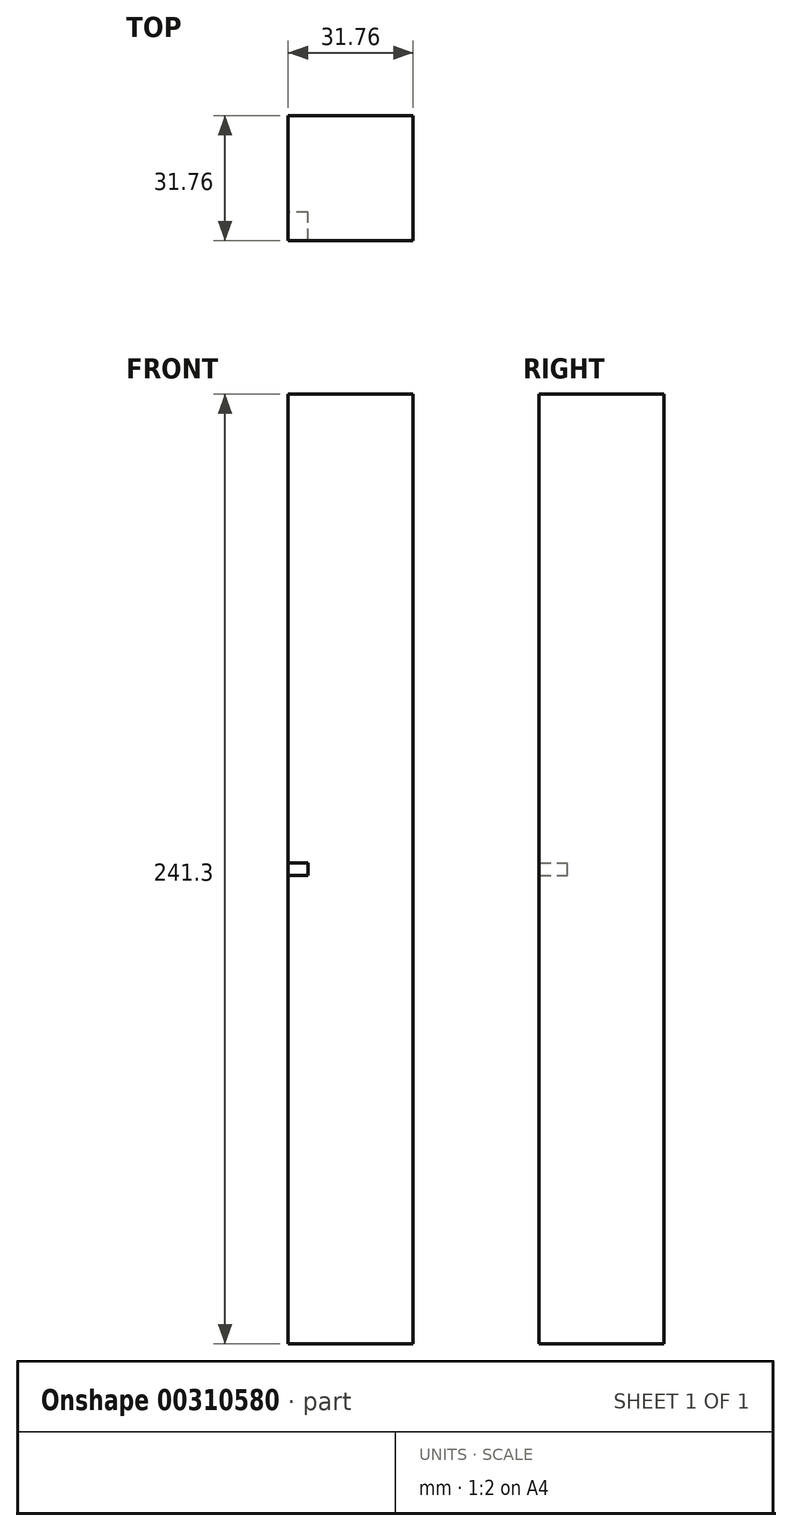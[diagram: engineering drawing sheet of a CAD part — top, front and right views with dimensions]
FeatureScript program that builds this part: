
annotation { "Feature Type Name" : "Feature", "Feature Type Description" : "" }
export const myFeature = defineFeature(function(context is Context, id is Id, definition is map)
    precondition{}
    {
        {
            var Q0;
            Q0=qCreatedBy(makeId("Top.planeOp"),FACE);
            var sketch = newSketch(context, id + "F0", { "sketchPlane" : qUnion([Q0])});
            skLineSegment(sketch, "E0.bottom", {"start": v(15.87, 15.88) * mm, "end": v(-15.88, 15.88) * mm});
            skLineSegment(sketch, "E0.top", {"start": v(15.88, -15.88) * mm, "end": v(-15.87, -15.88) * mm});
            skLineSegment(sketch, "E0.left", {"start": v(15.87, 15.88) * mm, "end": v(15.88, -15.88) * mm});
            skLineSegment(sketch, "E0.right", {"start": v(-15.88, 15.88) * mm, "end": v(-15.87, -15.88) * mm});
            skPoint(sketch, "E0.middle", {"position": v(0, 0) * mm});
            skSolve(sketch);
        }
        {
            var Q0;
            Q0=makeQuery(id+"F0.imprint","IMPRINT",FACE,{"disambiguationData":[TD([[makeQuery(id+"F0.imprint","IMPRINT",EDGE,{"derivedFrom":sQuery(id+"F0.wireOp",EDGE,"E0.bottom")}),1.0]])]});
            extrude(context, id + "F1", {"entities" : qUnion([Q0]), "depth" : 241.3 * mm, "symmetric" : true});
        }
        {
            var Q0;
            Q0=makeQuery(id+"F1.opExtrude","SWEPT_FACE",FACE,{"disambiguationData":[OSD([sQuery(id+"F0.wireOp",EDGE,"E0.right")])]});
            var sketch = newSketch(context, id + "F2", { "sketchPlane" : qUnion([Q0])});
            skLineSegment(sketch, "E1.top", {"start": v(15.87, 1.59) * mm, "end": v(8.7, 1.59) * mm});
            skLineSegment(sketch, "E1.left", {"start": v(15.87, 0) * mm, "end": v(15.87, 1.59) * mm});
            skLineSegment(sketch, "E1.right", {"start": v(8.7, 0) * mm, "end": v(8.7, 1.59) * mm});
            skLineSegment(sketch, "E2.MirrorCS", {"start": v(15.87, -1.59) * mm, "end": v(8.7, -1.59) * mm});
            skLineSegment(sketch, "E3.MirrorCS", {"start": v(8.7, 0) * mm, "end": v(8.7, -1.59) * mm});
            skLineSegment(sketch, "E4.MirrorCS", {"start": v(15.87, 0) * mm, "end": v(15.87, -1.59) * mm});
            skSolve(sketch);
        }
        {
            var Q0;
            Q0=makeQuery(id+"F2.imprint","IMPRINT",FACE,{"disambiguationData":[TD([[makeQuery(id+"F2.imprint","IMPRINT",EDGE,{"derivedFrom":sQuery(id+"F2.wireOp",EDGE,"E1.top")}),1.0]])]});
            extrude(context, id + "F3", {"entities" : qUnion([Q0]), "operationType" : NewBodyOperationType.REMOVE, "oppositeDirection" : true, "depth" : 5.08 * mm});
        }
    });
